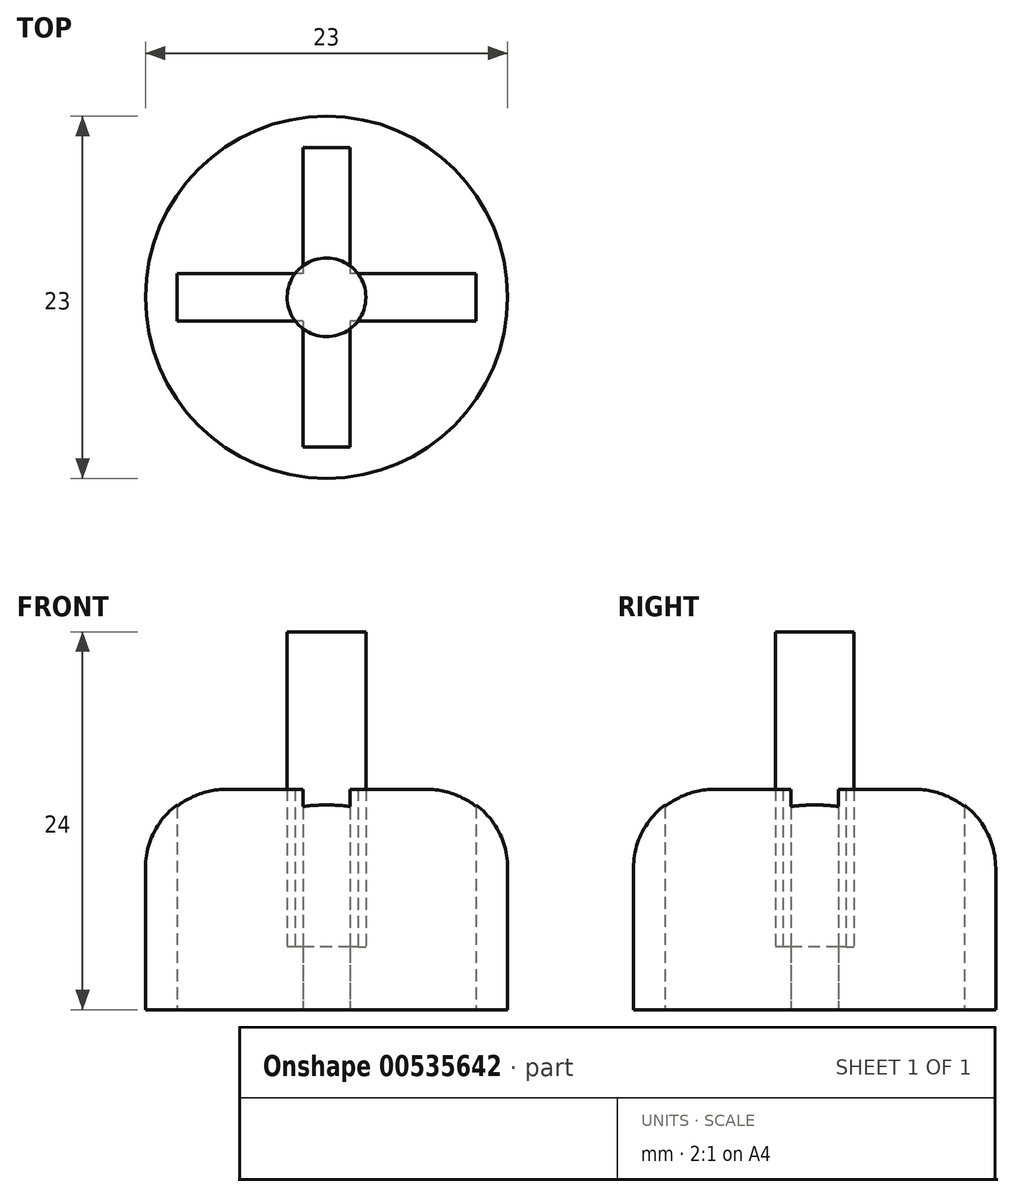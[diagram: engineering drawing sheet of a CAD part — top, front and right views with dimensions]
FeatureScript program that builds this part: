
annotation { "Feature Type Name" : "Feature", "Feature Type Description" : "" }
export const myFeature = defineFeature(function(context is Context, id is Id, definition is map)
    precondition{}
    {
        {
            var Q0;
            Q0=qCreatedBy(makeId("Top.planeOp"),FACE);
            var sketch = newSketch(context, id + "F0", { "sketchPlane" : qUnion([Q0])});
            skCircle(sketch, "E0", {"center": v(0, 0) * mm, "radius": 11.5 * mm});
            skLineSegment(sketch, "E1", {"start": v(0, -9.5) * mm, "end": v(0, 9.5) * mm, "construction": true});
            skLineSegment(sketch, "E2", {"start": v(-9.5, 0) * mm, "end": v(9.5, 0) * mm, "construction": true});
            skLineSegment(sketch, "E3.bottom", {"start": v(9.5, -1.5) * mm, "end": v(-9.5, -1.5) * mm});
            skLineSegment(sketch, "E3.top", {"start": v(9.5, 1.5) * mm, "end": v(-9.5, 1.5) * mm});
            skLineSegment(sketch, "E3.left", {"start": v(9.5, -1.5) * mm, "end": v(9.5, 1.5) * mm});
            skLineSegment(sketch, "E3.right", {"start": v(-9.5, -1.5) * mm, "end": v(-9.5, 1.5) * mm});
            skLineSegment(sketch, "E4.bottom", {"start": v(1.5, 9.5) * mm, "end": v(-1.5, 9.5) * mm});
            skLineSegment(sketch, "E4.top", {"start": v(1.5, -9.5) * mm, "end": v(-1.5, -9.5) * mm});
            skLineSegment(sketch, "E4.left", {"start": v(1.5, 9.5) * mm, "end": v(1.5, -9.5) * mm});
            skLineSegment(sketch, "E4.right", {"start": v(-1.5, 9.5) * mm, "end": v(-1.5, -9.5) * mm});
            skSolve(sketch);
        }
        {
            var Q0;
            Q0=makeQuery(id+"F0.imprint","IMPRINT",FACE,{"disambiguationData":[TD([[makeQuery(id+"F0.imprint","IMPRINT",EDGE,{"derivedFrom":sQuery(id+"F0.wireOp",EDGE,"E0")}),1.0]])]});
            extrude(context, id + "F1", {"entities" : qUnion([Q0]), "depth" : 11 * mm, "offsetDistance" : 25 * mm});
        }
        {
            var Q0;
            Q0=makeQuery(id+"F1.opExtrude","CAP_FACE",FACE,{"disambiguationData":[OSD([sQuery(id+"F0.wireOp",EDGE,"E0"),sQuery(id+"F0.wireOp",EDGE,"E3.bottom"),sQuery(id+"F0.wireOp",EDGE,"E3.top"),sQuery(id+"F0.wireOp",EDGE,"E3.left"),sQuery(id+"F0.wireOp",EDGE,"E3.right"),sQuery(id+"F0.wireOp",EDGE,"E4.bottom"),sQuery(id+"F0.wireOp",EDGE,"E4.top"),sQuery(id+"F0.wireOp",EDGE,"E4.left"),sQuery(id+"F0.wireOp",EDGE,"E4.right")])],"isStart":false});
            var sketch = newSketch(context, id + "F2", { "sketchPlane" : qUnion([Q0])});
            skCircle(sketch, "E5", {"center": v(0, 0) * mm, "radius": 11.5 * mm});
            skSolve(sketch);
        }
        {
            var Q0;
            Q0=makeQuery(id+"F2.imprint","IMPRINT",FACE,{"disambiguationData":[TD([[makeQuery(id+"F2.imprint","IMPRINT",EDGE,{"derivedFrom":sQuery(id+"F2.wireOp",EDGE,"E5")}),1.0]])]});
            extrude(context, id + "F3", {"entities" : qUnion([Q0]), "operationType" : NewBodyOperationType.ADD, "depth" : 3 * mm, "offsetDistance" : 25 * mm});
        }
        {
            var Q0;
            Q0=makeQuery(id+"F3.opExtrude","CAP_EDGE",EDGE,{"disambiguationData":[OSD([sQuery(id+"F2.wireOp",EDGE,"E5")])],"isStart":false});
            fillet(context, id + "F4", {"entities" : qUnion([Q0]), "radius" : 5 * mm, "tangentPropagation" : true, "allowEdgeOverflow" : false});
        }
        {
            var Q0;
            Q0=makeQuery(id+"F4.opFillet","SPLIT",FACE,{"disambiguationData":[OD(1.0)],"derivedFrom":makeQuery(id+"F3.opExtrude","CAP_FACE",FACE,{"disambiguationData":[OSD([sQuery(id+"F0.wireOp",EDGE,"E3.bottom"),sQuery(id+"F0.wireOp",EDGE,"E3.top"),sQuery(id+"F0.wireOp",EDGE,"E3.left"),sQuery(id+"F0.wireOp",EDGE,"E3.right"),sQuery(id+"F0.wireOp",EDGE,"E4.bottom"),sQuery(id+"F0.wireOp",EDGE,"E4.top"),sQuery(id+"F0.wireOp",EDGE,"E4.left"),sQuery(id+"F0.wireOp",EDGE,"E4.right"),sQuery(id+"F2.wireOp",EDGE,"E5")])],"isStart":false})});
            var sketch = newSketch(context, id + "F5", { "sketchPlane" : qUnion([Q0])});
            skCircle(sketch, "E6", {"center": v(0, 0) * mm, "radius": 2.5 * mm});
            skSolve(sketch);
        }
        {
            var Q0;
            {var subQ0=sQuery(id+"F5.wireOp",EDGE,"E6");var subQ1=sQuery(id+"F0.wireOp",EDGE,"E3.top");var subQ4=makeQuery(id+"F3.opExtrude","CAP_EDGE",EDGE,{"disambiguationData":[OSD([subQ1]),TDD([makeQuery(id+"F2.imprint","IMPRINT",EDGE,{"derivedFrom":makeQuery(id+"F1.opExtrude","CAP_EDGE",EDGE,{"disambiguationData":[OSD([subQ1]),TDD([makeQuery(id+"F0.imprint","IMPRINT",EDGE,{"disambiguationData":[TD([[makeQuery(id+"F0.imprint","INTERSECT",VERTEX,{"derivedFrom":[subQ1,sQuery(id+"F0.wireOp",EDGE,"E3.left")]}),-1.0]])],"derivedFrom":subQ1})])],"isStart":false})})])],"isStart":false});var subQ5=makeQuery(id+"F5.imprint","INTERSECT",VERTEX,{"derivedFrom":[subQ4,subQ0]});Q0=makeQuery(id+"F5.imprint","IMPRINT",FACE,{"disambiguationData":[TD([[makeQuery(id+"F5.imprint","IMPRINT",EDGE,{"disambiguationData":[TD([[subQ5,1.0]])],"derivedFrom":subQ0}),1.0]])]});}
            extrude(context, id + "F6", {"entities" : qUnion([Q0]), "operationType" : NewBodyOperationType.ADD, "endBound" : BoundingType.SYMMETRIC, "depth" : 20 * mm, "offsetDistance" : 25 * mm});
        }
    });
